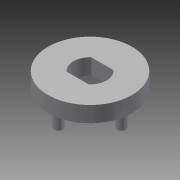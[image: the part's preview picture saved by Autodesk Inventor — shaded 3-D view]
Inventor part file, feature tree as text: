
AUTODESK INVENTOR PART (.ipt)
format: ipt  version: 2014 SP1 (Build 180222100, 222)  size: 135,168 bytes
history: native  units: in
note: dims shown in document units (in); Inventor stores cm internally (conversion verified against a paired STEP export)
features: extrude x2, sketch x1
ambient origin geometry x8: Origin, YZ Plane, XZ Plane, XY Plane, X Axis, Y Axis, Z Axis, Center Point
bodies: Solid1 (feature_tree)
feature tree (3):
  sketch  "Sketch1"  dims[d1=0.35in d2=0.7087in d3=0.9449in d4=0.0984in d5=1.5748in d7=360.0deg d9=0.1772in d10=0.0in d11=0.1969in d12=0.0in d13=0.375in d14=0.25in]
  extrude  "Extrusion1"  Depth=0.1969in
  extrude  "Extrusion2"  Depth=0.1969in
